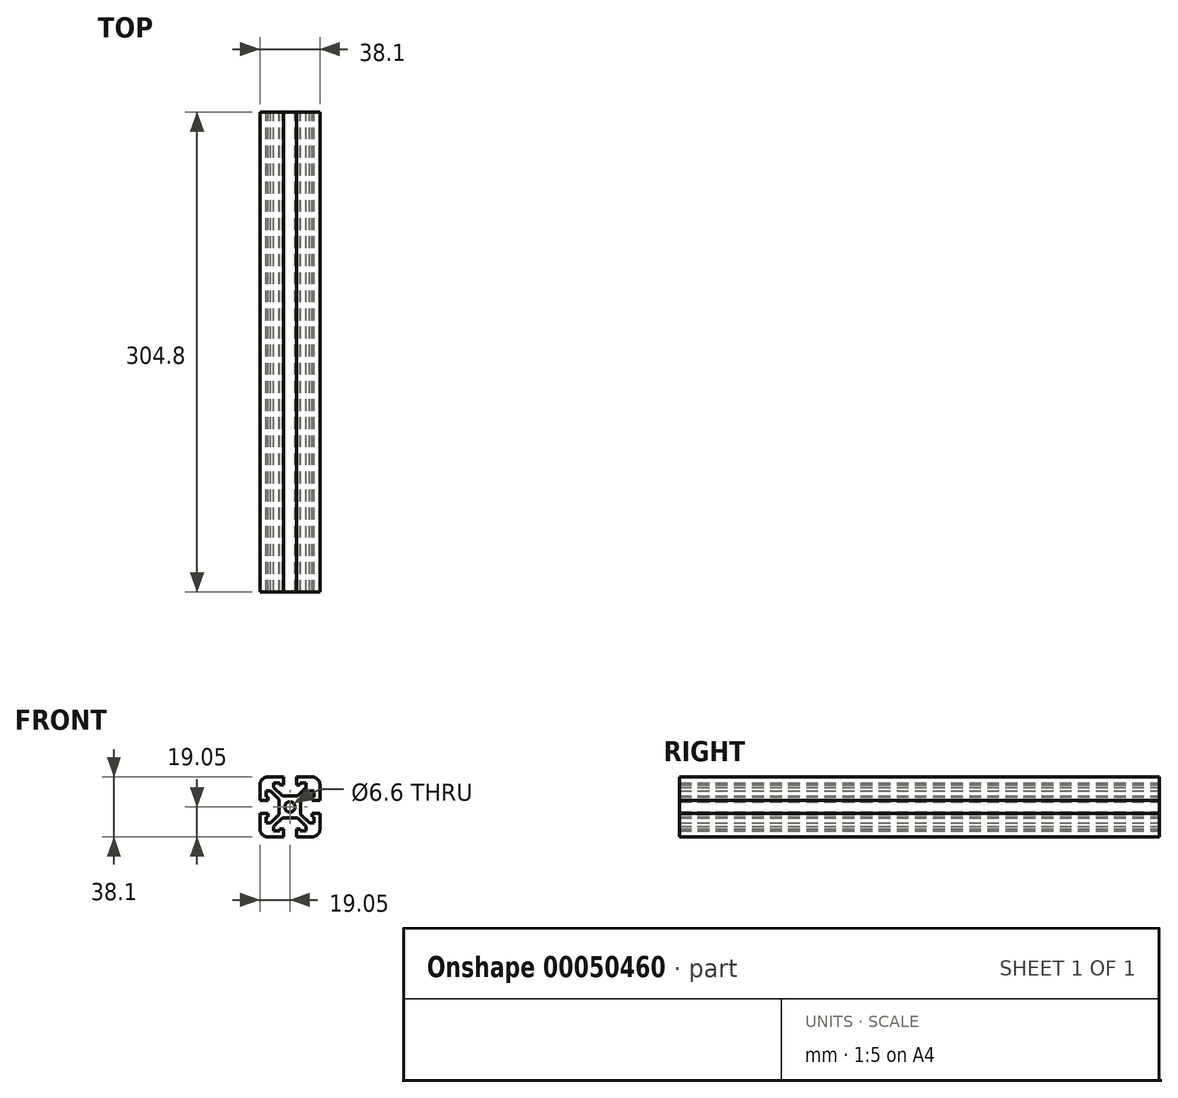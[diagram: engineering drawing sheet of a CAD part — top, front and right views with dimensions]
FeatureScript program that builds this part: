
annotation { "Feature Type Name" : "Feature", "Feature Type Description" : "" }
export const myFeature = defineFeature(function(context is Context, id is Id, definition is map)
    precondition{}
    {
        {
            var Q0;
            Q0=qCreatedBy(makeId("Front.planeOp"),FACE);
            var sketch = newSketch(context, id + "F0", { "sketchPlane" : qUnion([Q0])});
            skLineSegment(sketch, "E0.bottom", {"start": v(6.86, 6.86) * mm, "end": v(-6.86, 6.86) * mm, "construction": true});
            skLineSegment(sketch, "E0.top", {"start": v(6.86, -6.86) * mm, "end": v(-6.86, -6.86) * mm, "construction": true});
            skLineSegment(sketch, "E0.left", {"start": v(6.86, 6.86) * mm, "end": v(6.86, -6.86) * mm, "construction": true});
            skLineSegment(sketch, "E0.right", {"start": v(-6.86, 6.86) * mm, "end": v(-6.86, -6.86) * mm, "construction": true});
            skPoint(sketch, "E0.middle", {"position": v(0, 0) * mm});
            skLineSegment(sketch, "E1.bottom", {"start": v(-19.05, -19.05) * mm, "end": v(19.05, -19.05) * mm});
            skLineSegment(sketch, "E1.top", {"start": v(-19.05, 19.05) * mm, "end": v(19.05, 19.05) * mm});
            skLineSegment(sketch, "E1.left", {"start": v(-19.05, -19.05) * mm, "end": v(-19.05, 19.05) * mm});
            skLineSegment(sketch, "E1.right", {"start": v(19.05, -19.05) * mm, "end": v(19.05, 19.05) * mm});
            skSolve(sketch);
        }
        {
            var Q0;
            Q0=qCreatedBy(makeId("Front.planeOp"),FACE);
            var sketch = newSketch(context, id + "F1", { "sketchPlane" : qUnion([Q0])});
            skLineSegment(sketch, "E2.right", {"start": v(4.06, 19.05) * mm, "end": v(4.06, 13.97) * mm});
            skLineSegment(sketch, "E3", {"start": v(0, 0) * mm, "end": v(20.66, 20.66) * mm, "construction": true});
            skLineSegment(sketch, "E4", {"start": v(0, 2.16) * mm, "end": v(20.57, 22.73) * mm, "construction": true});
            skLineSegment(sketch, "E5", {"start": v(4.06, 6.86) * mm, "end": v(4.7, 6.86) * mm});
            skLineSegment(sketch, "E6", {"start": v(10.29, 40.49) * mm, "end": v(10.29, -4.2) * mm, "construction": true});
            skLineSegment(sketch, "E7", {"start": v(4.7, 6.86) * mm, "end": v(10.29, 12.44) * mm});
            skLineSegment(sketch, "E8", {"start": v(4.06, 13.97) * mm, "end": v(6.48, 13.97) * mm});
            skLineSegment(sketch, "E9", {"start": v(10.29, 13.97) * mm, "end": v(10.29, 12.44) * mm});
            skLineSegment(sketch, "E10.MirrorCS", {"start": v(19.05, 4.06) * mm, "end": v(13.97, 4.06) * mm});
            skLineSegment(sketch, "E11.MirrorCS", {"start": v(6.86, 0) * mm, "end": v(6.86, 4.06) * mm});
            skLineSegment(sketch, "E12.MirrorCS", {"start": v(13.97, 4.06) * mm, "end": v(13.97, 6.48) * mm});
            skLineSegment(sketch, "E13.MirrorCS", {"start": v(6.86, 4.7) * mm, "end": v(12.44, 10.29) * mm});
            skLineSegment(sketch, "E14.MirrorCS", {"start": v(13.97, 10.29) * mm, "end": v(12.44, 10.29) * mm});
            skLineSegment(sketch, "E15.MirrorCS", {"start": v(6.86, 4.06) * mm, "end": v(6.86, 4.7) * mm});
            skLineSegment(sketch, "E16.top", {"start": v(10.29, 15.24) * mm, "end": v(6.48, 15.24) * mm});
            skLineSegment(sketch, "E16.left", {"start": v(10.29, 13.97) * mm, "end": v(10.29, 15.24) * mm});
            skLineSegment(sketch, "E16.right", {"start": v(6.48, 13.97) * mm, "end": v(6.48, 15.24) * mm});
            skLineSegment(sketch, "E17.MirrorCS", {"start": v(15.24, 10.29) * mm, "end": v(15.24, 6.48) * mm});
            skLineSegment(sketch, "E18.MirrorCS", {"start": v(13.97, 6.48) * mm, "end": v(15.24, 6.48) * mm});
            skLineSegment(sketch, "E19.MirrorCS", {"start": v(13.97, 10.29) * mm, "end": v(15.24, 10.29) * mm});
            skPoint(sketch, "E20.orphan", {"position": v(13.97, 10.29) * mm});
            skLineSegment(sketch, "E21.MirrorCS", {"start": v(-13.97, 10.29) * mm, "end": v(-15.24, 10.29) * mm});
            skLineSegment(sketch, "E22.MirrorCS", {"start": v(-10.29, 13.97) * mm, "end": v(-10.29, 12.44) * mm});
            skLineSegment(sketch, "E23.MirrorCS", {"start": v(-13.97, 10.29) * mm, "end": v(-12.44, 10.29) * mm});
            skLineSegment(sketch, "E24.MirrorCS", {"start": v(-4.06, 13.97) * mm, "end": v(-6.48, 13.97) * mm});
            skLineSegment(sketch, "E25.MirrorCS", {"start": v(-4.06, 6.86) * mm, "end": v(-4.7, 6.86) * mm});
            skLineSegment(sketch, "E26.MirrorCS", {"start": v(-6.48, 13.97) * mm, "end": v(-6.48, 15.24) * mm});
            skLineSegment(sketch, "E27.MirrorCS", {"start": v(-13.97, 6.48) * mm, "end": v(-15.24, 6.48) * mm});
            skLineSegment(sketch, "E28.MirrorCS", {"start": v(-6.86, 4.06) * mm, "end": v(-6.86, 4.7) * mm});
            skLineSegment(sketch, "E29.MirrorCS", {"start": v(-10.29, 13.97) * mm, "end": v(-10.29, 15.24) * mm});
            skLineSegment(sketch, "E30.MirrorCS", {"start": v(-4.7, 6.86) * mm, "end": v(-10.29, 12.44) * mm});
            skLineSegment(sketch, "E31.MirrorCS", {"start": v(-19.05, 4.06) * mm, "end": v(-13.97, 4.06) * mm});
            skLineSegment(sketch, "E32.MirrorCS", {"start": v(-13.97, 4.06) * mm, "end": v(-13.97, 6.48) * mm});
            skPoint(sketch, "E33.MirrorP", {"position": v(-13.97, 10.29) * mm});
            skLineSegment(sketch, "E34.MirrorCS", {"start": v(0, 0) * mm, "end": v(-20.66, 20.66) * mm, "construction": true});
            skLineSegment(sketch, "E35.MirrorCS", {"start": v(0, 2.16) * mm, "end": v(-20.57, 22.73) * mm, "construction": true});
            skLineSegment(sketch, "E36.MirrorCS", {"start": v(-4.06, 19.05) * mm, "end": v(-4.06, 13.97) * mm});
            skLineSegment(sketch, "E37.MirrorCS", {"start": v(-6.86, 0) * mm, "end": v(-6.86, 4.06) * mm});
            skLineSegment(sketch, "E38.MirrorCS", {"start": v(-6.86, 4.7) * mm, "end": v(-12.44, 10.29) * mm});
            skLineSegment(sketch, "E39.MirrorCS", {"start": v(-10.29, 15.24) * mm, "end": v(-6.48, 15.24) * mm});
            skLineSegment(sketch, "E40.MirrorCS", {"start": v(-15.24, 10.29) * mm, "end": v(-15.24, 6.48) * mm});
            skLineSegment(sketch, "E41.MirrorCS", {"start": v(13.97, -10.29) * mm, "end": v(15.24, -10.29) * mm});
            skLineSegment(sketch, "E42.MirrorCS", {"start": v(13.97, -6.48) * mm, "end": v(15.24, -6.48) * mm});
            skLineSegment(sketch, "E43.MirrorCS", {"start": v(13.97, -4.06) * mm, "end": v(13.97, -6.48) * mm});
            skLineSegment(sketch, "E44.MirrorCS", {"start": v(10.29, -13.97) * mm, "end": v(10.29, -12.44) * mm});
            skLineSegment(sketch, "E45.MirrorCS", {"start": v(4.06, -13.97) * mm, "end": v(6.48, -13.97) * mm});
            skLineSegment(sketch, "E46.MirrorCS", {"start": v(-4.06, -6.86) * mm, "end": v(-4.7, -6.86) * mm});
            skLineSegment(sketch, "E47.MirrorCS", {"start": v(-13.97, -6.48) * mm, "end": v(-15.24, -6.48) * mm});
            skLineSegment(sketch, "E48.MirrorCS", {"start": v(-6.86, -4.06) * mm, "end": v(-6.86, -4.7) * mm});
            skLineSegment(sketch, "E49.MirrorCS", {"start": v(-13.97, -10.29) * mm, "end": v(-15.24, -10.29) * mm});
            skLineSegment(sketch, "E50.MirrorCS", {"start": v(6.86, -4.06) * mm, "end": v(6.86, -4.7) * mm});
            skLineSegment(sketch, "E51.MirrorCS", {"start": v(13.97, -10.29) * mm, "end": v(12.44, -10.29) * mm});
            skLineSegment(sketch, "E52.MirrorCS", {"start": v(10.29, -13.97) * mm, "end": v(10.29, -15.24) * mm});
            skLineSegment(sketch, "E53.MirrorCS", {"start": v(-10.29, -13.97) * mm, "end": v(-10.29, -12.44) * mm});
            skLineSegment(sketch, "E54.MirrorCS", {"start": v(-10.29, -13.97) * mm, "end": v(-10.29, -15.24) * mm});
            skLineSegment(sketch, "E55.MirrorCS", {"start": v(4.06, -6.86) * mm, "end": v(4.7, -6.86) * mm});
            skLineSegment(sketch, "E56.MirrorCS", {"start": v(-13.97, -10.29) * mm, "end": v(-12.44, -10.29) * mm});
            skLineSegment(sketch, "E57.MirrorCS", {"start": v(6.48, -13.97) * mm, "end": v(6.48, -15.24) * mm});
            skLineSegment(sketch, "E58.MirrorCS", {"start": v(-6.48, -13.97) * mm, "end": v(-6.48, -15.24) * mm});
            skLineSegment(sketch, "E59.MirrorCS", {"start": v(-13.97, -4.06) * mm, "end": v(-13.97, -6.48) * mm});
            skLineSegment(sketch, "E60.MirrorCS", {"start": v(-19.05, -4.06) * mm, "end": v(-13.97, -4.06) * mm});
            skLineSegment(sketch, "E61.MirrorCS", {"start": v(19.05, -4.06) * mm, "end": v(13.97, -4.06) * mm});
            skLineSegment(sketch, "E62.MirrorCS", {"start": v(-4.7, -6.86) * mm, "end": v(-10.29, -12.44) * mm});
            skPoint(sketch, "E63.MirrorP", {"position": v(-13.97, -10.29) * mm});
            skLineSegment(sketch, "E64.MirrorCS", {"start": v(0, -6.86) * mm, "end": v(4.06, -6.86) * mm});
            skLineSegment(sketch, "E65.MirrorCS", {"start": v(-4.06, -13.97) * mm, "end": v(-6.48, -13.97) * mm});
            skLineSegment(sketch, "E66.MirrorCS", {"start": v(0, -6.86) * mm, "end": v(-4.06, -6.86) * mm});
            skLineSegment(sketch, "E67.MirrorCS", {"start": v(4.7, -6.86) * mm, "end": v(10.29, -12.44) * mm});
            skLineSegment(sketch, "E68.MirrorCS", {"start": v(0, -2.16) * mm, "end": v(-16.9, -19.05) * mm, "construction": true});
            skLineSegment(sketch, "E69.MirrorCS", {"start": v(0, 0) * mm, "end": v(-19.05, -19.05) * mm, "construction": true});
            skLineSegment(sketch, "E70.MirrorCS", {"start": v(-6.86, -4.7) * mm, "end": v(-12.44, -10.29) * mm});
            skLineSegment(sketch, "E71.MirrorCS", {"start": v(6.86, 0) * mm, "end": v(6.86, -4.06) * mm});
            skPoint(sketch, "E72.MirrorP", {"position": v(13.97, -10.29) * mm});
            skLineSegment(sketch, "E73.MirrorCS", {"start": v(-15.24, -10.29) * mm, "end": v(-15.24, -6.48) * mm});
            skLineSegment(sketch, "E74.MirrorCS", {"start": v(-6.86, 0) * mm, "end": v(-6.86, -4.06) * mm});
            skLineSegment(sketch, "E75.MirrorCS", {"start": v(10.29, -15.24) * mm, "end": v(6.48, -15.24) * mm});
            skLineSegment(sketch, "E76.MirrorCS", {"start": v(6.86, -4.7) * mm, "end": v(12.44, -10.29) * mm});
            skLineSegment(sketch, "E77.MirrorCS", {"start": v(-10.29, -15.24) * mm, "end": v(-6.48, -15.24) * mm});
            skLineSegment(sketch, "E78.MirrorCS", {"start": v(4.06, -19.05) * mm, "end": v(4.06, -13.97) * mm});
            skLineSegment(sketch, "E79.MirrorCS", {"start": v(-4.06, -19.05) * mm, "end": v(-4.06, -13.97) * mm});
            skLineSegment(sketch, "E80.MirrorCS", {"start": v(15.24, -10.29) * mm, "end": v(15.24, -6.48) * mm});
            skPoint(sketch, "E81.start.orphan", {"position": v(0, 40.6) * mm});
            skLineSegment(sketch, "E82.trimOffspring", {"start": v(19.05, 0) * mm, "end": v(30, 0) * mm, "construction": true});
            skLineSegment(sketch, "E83.trimOffspring", {"start": v(-6.86, 0) * mm, "end": v(10.29, 0) * mm, "construction": true});
            skLineSegment(sketch, "E84", {"start": v(-4.06, 6.86) * mm, "end": v(4.06, 6.86) * mm});
            skLineSegment(sketch, "E85.bottom", {"start": v(19.05, 19.05) * mm, "end": v(4.06, 19.05) * mm});
            skLineSegment(sketch, "E85.top", {"start": v(19.05, -19.05) * mm, "end": v(4.06, -19.05) * mm});
            skLineSegment(sketch, "E85.left", {"start": v(19.05, 19.05) * mm, "end": v(19.05, 4.06) * mm});
            skLineSegment(sketch, "E85.right", {"start": v(-19.05, 19.05) * mm, "end": v(-19.05, 4.06) * mm});
            skPoint(sketch, "E85.middle", {"position": v(0, 0) * mm});
            skLineSegment(sketch, "E86.trimOffspring", {"start": v(-4.06, 19.05) * mm, "end": v(-19.05, 19.05) * mm});
            skLineSegment(sketch, "E87.trimOffspring", {"start": v(-19.05, -4.06) * mm, "end": v(-19.05, -19.05) * mm});
            skPoint(sketch, "E88.start.orphan", {"position": v(-32.43, 0) * mm});
            skPoint(sketch, "E89.MirrorCS.end.orphan", {"position": v(19.05, 4.06) * mm});
            skLineSegment(sketch, "E90.trimOffspring", {"start": v(19.05, -4.06) * mm, "end": v(19.05, -19.05) * mm});
            skLineSegment(sketch, "E91.trimOffspring", {"start": v(-4.06, -19.05) * mm, "end": v(-19.05, -19.05) * mm});
            skSolve(sketch);
        }
        {
            var Q0;
            Q0=qCreatedBy(makeId("Front.planeOp"),FACE);
            var sketch = newSketch(context, id + "F2", { "sketchPlane" : qUnion([Q0])});
            skCircle(sketch, "E92", {"center": v(0, 0) * mm, "radius": 3.3 * mm});
            skSolve(sketch);
        }
        {
            var Q0;
            Q0 = qSketchRegion(id + "F1", true);
            extrude(context, id + "F3", {"entities" : qUnion([Q0]), "depth" : 304.8 * mm});
        }
        {
            var Q0;
            Q0 = qSketchRegion(id + "F2", true);
            extrude(context, id + "F4", {"entities" : qUnion([Q0]), "operationType" : NewBodyOperationType.REMOVE, "endBound" : BoundingType.THROUGH_ALL, "depth" : 25.4 * mm});
        }
        {
            var Q0;
            Q0=makeQuery(id+"F3.opExtrude","SWEPT_EDGE",EDGE,{"disambiguationData":[OSD([sQuery(id+"F1.wireOp",EDGE,"E85.bottom"),sQuery(id+"F1.wireOp",EDGE,"E85.left")])]});
            var Q1;
            Q1=makeQuery(id+"F3.opExtrude","SWEPT_EDGE",EDGE,{"disambiguationData":[OSD([sQuery(id+"F1.wireOp",EDGE,"E85.right"),sQuery(id+"F1.wireOp",EDGE,"E86.trimOffspring")])]});
            var Q2;
            Q2=makeQuery(id+"F3.opExtrude","SWEPT_EDGE",EDGE,{"disambiguationData":[OSD([sQuery(id+"F1.wireOp",EDGE,"E85.top"),sQuery(id+"F1.wireOp",EDGE,"E90.trimOffspring")])]});
            var Q3;
            Q3=makeQuery(id+"F3.opExtrude","SWEPT_EDGE",EDGE,{"disambiguationData":[OSD([sQuery(id+"F1.wireOp",EDGE,"E87.trimOffspring"),sQuery(id+"F1.wireOp",EDGE,"E91.trimOffspring")])]});
            fillet(context, id + "F5", {"entities" : qUnion([Q0, Q1, Q2, Q3]), "radius" : 5.08 * mm, "tangentPropagation" : true, "allowEdgeOverflow" : false});
        }
    });
